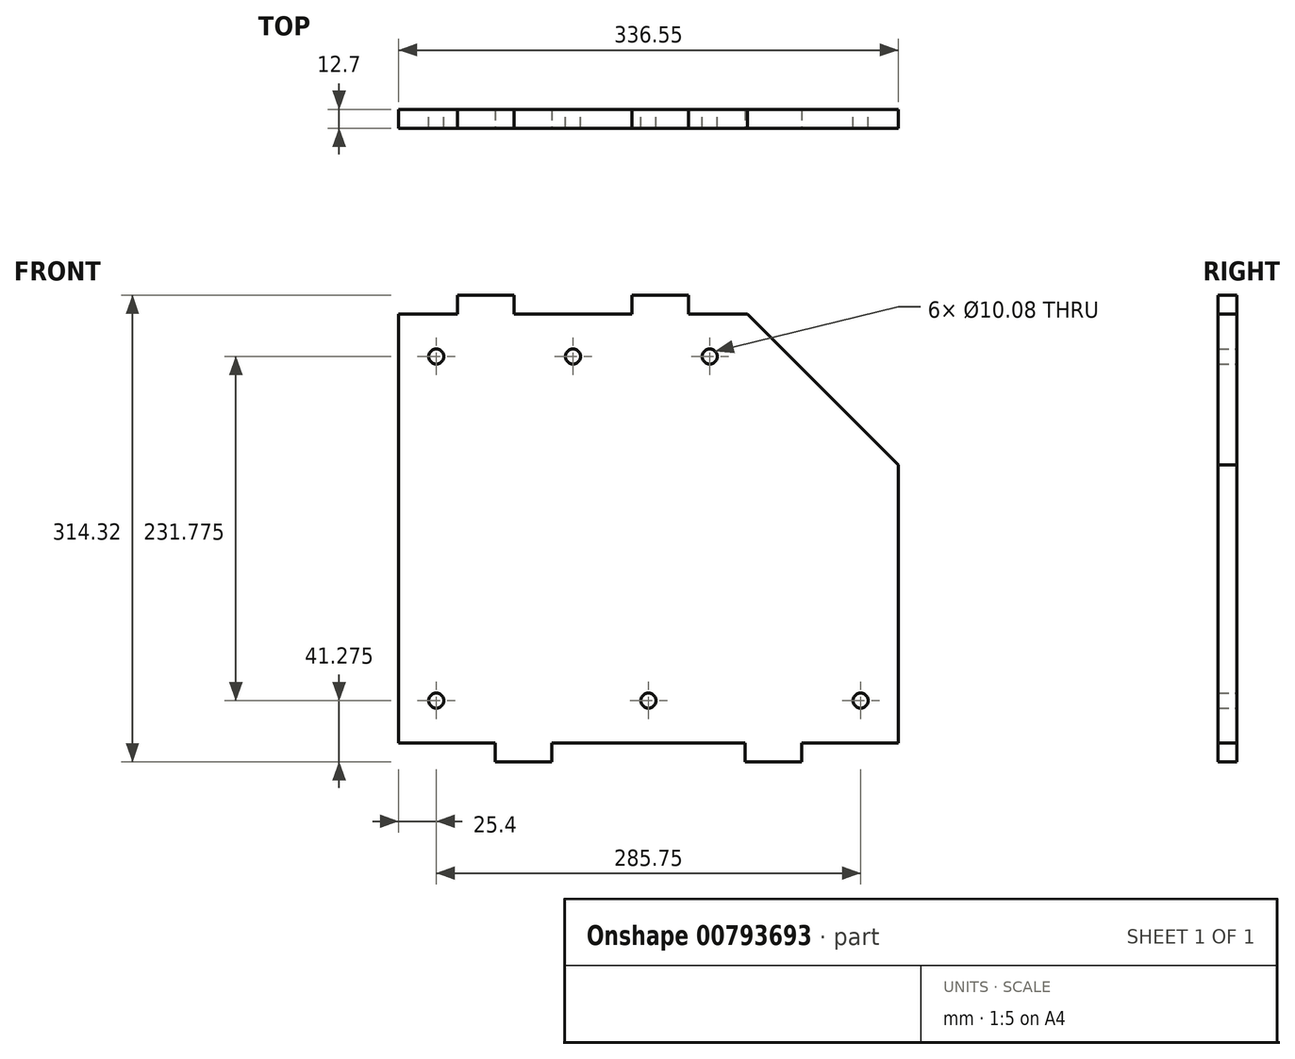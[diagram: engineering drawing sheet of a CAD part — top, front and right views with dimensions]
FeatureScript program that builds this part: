
annotation { "Feature Type Name" : "Feature", "Feature Type Description" : "" }
export const myFeature = defineFeature(function(context is Context, id is Id, definition is map)
    precondition{}
    {
        {
            var Q0;
            Q0=qCreatedBy(makeId("Front.planeOp"),FACE);
            var sketch = newSketch(context, id + "F0", { "sketchPlane" : qUnion([Q0])});
            skLineSegment(sketch, "E0", {"start": v(0, 0) * mm, "end": v(0, 288.92) * mm});
            skLineSegment(sketch, "E1", {"start": v(0, 288.93) * mm, "end": v(234.95, 288.93) * mm});
            skLineSegment(sketch, "E2", {"start": v(234.95, 288.93) * mm, "end": v(336.55, 187.33) * mm});
            skLineSegment(sketch, "E3", {"start": v(336.55, 187.33) * mm, "end": v(336.55, 0) * mm});
            skLineSegment(sketch, "E4", {"start": v(336.55, 0) * mm, "end": v(0, 0) * mm});
            skLineSegment(sketch, "E5", {"start": v(0, 28.57) * mm, "end": v(336.55, 28.58) * mm, "construction": true});
            skLineSegment(sketch, "E6", {"start": v(0, 260.35) * mm, "end": v(263.53, 260.35) * mm, "construction": true});
            skPoint(sketch, "E7", {"position": v(117.48, 260.35) * mm});
            skPoint(sketch, "E8", {"position": v(168.28, 28.57) * mm});
            skPoint(sketch, "E9", {"position": v(209.55, 260.35) * mm});
            skPoint(sketch, "E10", {"position": v(25.4, 260.35) * mm});
            skPoint(sketch, "E11", {"position": v(311.15, 28.58) * mm});
            skPoint(sketch, "E12", {"position": v(25.4, 28.57) * mm});
            skSolve(sketch);
        }
        {
            var Q0;
            Q0 = qSketchRegion(id + "F0", true);
            extrude(context, id + "F1", {"entities" : qUnion([Q0]), "depth" : 12.7 * mm, "offsetDistance" : 25.4 * mm});
        }
        {
            var Q0;
            Q0=sQuery(id+"F0.wireOp",VERTEX,"E11");
            var Q1;
            Q1=sQuery(id+"F0.wireOp",VERTEX,"E8");
            var Q2;
            Q2=sQuery(id+"F0.wireOp",VERTEX,"E12");
            var Q3;
            Q3=sQuery(id+"F0.wireOp",VERTEX,"E10");
            var Q4;
            Q4=sQuery(id+"F0.wireOp",VERTEX,"E9");
            var Q5;
            Q5=sQuery(id+"F0.wireOp",VERTEX,"E7");
            var Q6;
            Q6=makeQuery(id+"F1.opExtrude","SWEPT_BODY",BODY,{"disambiguationData":[OSD([sQuery(id+"F0.wireOp",EDGE,"E0"),sQuery(id+"F0.wireOp",EDGE,"E1"),sQuery(id+"F0.wireOp",EDGE,"E2"),sQuery(id+"F0.wireOp",EDGE,"E3"),sQuery(id+"F0.wireOp",EDGE,"E4")])]});
            hole(context, id + "F2", {"style" : HoleStyle.SIMPLE, "endStyle" : HoleEndStyle.THROUGH, "oppositeDirection" : true, "standardTappedOrClearance" : lookupTablePath({ "fit" : "Normal (ASME)", "standard" : "ANSI", "size" : "3/8", "type" : "Clearance" }), "standardBlindInLast" : lookupTablePath({ "fit" : "Free", "standard" : "ANSI", "size" : "3/8", "type" : "Clearance" }), "holeDiameter" : 10.08 * mm, "majorDiameter" : 6.35 * mm, "isTappedThrough" : true, "tappedDepth" : 12.7 * mm, "tapClearance" : 3, "locations" : qUnion([Q0, Q1, Q2, Q3, Q4, Q5]), "scope" : qUnion([Q6])});
        }
        {
            var Q0;
            Q0=makeQuery(id+"F1.opExtrude","CAP_FACE",FACE,{"disambiguationData":[OSD([sQuery(id+"F0.wireOp",EDGE,"E0"),sQuery(id+"F0.wireOp",EDGE,"E1"),sQuery(id+"F0.wireOp",EDGE,"E2"),sQuery(id+"F0.wireOp",EDGE,"E3"),sQuery(id+"F0.wireOp",EDGE,"E4")])],"isStart":false});
            var sketch = newSketch(context, id + "F3", { "sketchPlane" : qUnion([Q0])});
            skLineSegment(sketch, "E13", {"start": v(117.47, 288.93) * mm, "end": v(117.47, 0) * mm, "construction": true});
            skPoint(sketch, "E13.endSnap0", {"position": v(117.47, 288.93) * mm});
            skLineSegment(sketch, "E14.bottom", {"start": v(39.69, 288.93) * mm, "end": v(77.79, 288.93) * mm});
            skLineSegment(sketch, "E14.top", {"start": v(39.69, 301.63) * mm, "end": v(77.79, 301.63) * mm});
            skLineSegment(sketch, "E14.left", {"start": v(39.69, 288.93) * mm, "end": v(39.69, 301.63) * mm});
            skLineSegment(sketch, "E14.right", {"start": v(77.79, 288.93) * mm, "end": v(77.79, 301.63) * mm});
            skLineSegment(sketch, "E15.bottom", {"start": v(157.16, 288.93) * mm, "end": v(195.26, 288.93) * mm});
            skLineSegment(sketch, "E15.top", {"start": v(157.16, 301.63) * mm, "end": v(195.26, 301.63) * mm});
            skLineSegment(sketch, "E15.left", {"start": v(157.16, 288.93) * mm, "end": v(157.16, 301.63) * mm});
            skLineSegment(sketch, "E15.right", {"start": v(195.26, 288.93) * mm, "end": v(195.26, 301.63) * mm});
            skLineSegment(sketch, "E16", {"start": v(168.28, 0) * mm, "end": v(168.28, 288.93) * mm, "construction": true});
            skLineSegment(sketch, "E17.bottom", {"start": v(65.09, 0) * mm, "end": v(103.19, 0) * mm});
            skLineSegment(sketch, "E17.top", {"start": v(65.09, -12.7) * mm, "end": v(103.19, -12.7) * mm});
            skLineSegment(sketch, "E17.left", {"start": v(65.09, 0) * mm, "end": v(65.09, -12.7) * mm});
            skLineSegment(sketch, "E17.right", {"start": v(103.19, 0) * mm, "end": v(103.19, -12.7) * mm});
            skLineSegment(sketch, "E18.MirrorCS", {"start": v(271.46, 0) * mm, "end": v(271.46, -12.7) * mm});
            skLineSegment(sketch, "E19.MirrorCS", {"start": v(296.86, 288.93) * mm, "end": v(258.76, 288.93) * mm});
            skLineSegment(sketch, "E20.MirrorCS", {"start": v(271.46, 0) * mm, "end": v(233.36, 0) * mm});
            skLineSegment(sketch, "E21.MirrorCS", {"start": v(271.46, -12.7) * mm, "end": v(233.36, -12.7) * mm});
            skLineSegment(sketch, "E22.MirrorCS", {"start": v(233.36, 0) * mm, "end": v(233.36, -12.7) * mm});
            skSolve(sketch);
        }
        {
            var Q0;
            Q0 = qSketchRegion(id + "F3", true);
            extrude(context, id + "F4", {"entities" : qUnion([Q0]), "operationType" : NewBodyOperationType.ADD, "oppositeDirection" : true, "depth" : 12.7 * mm, "offsetDistance" : 25.4 * mm});
        }
    });
